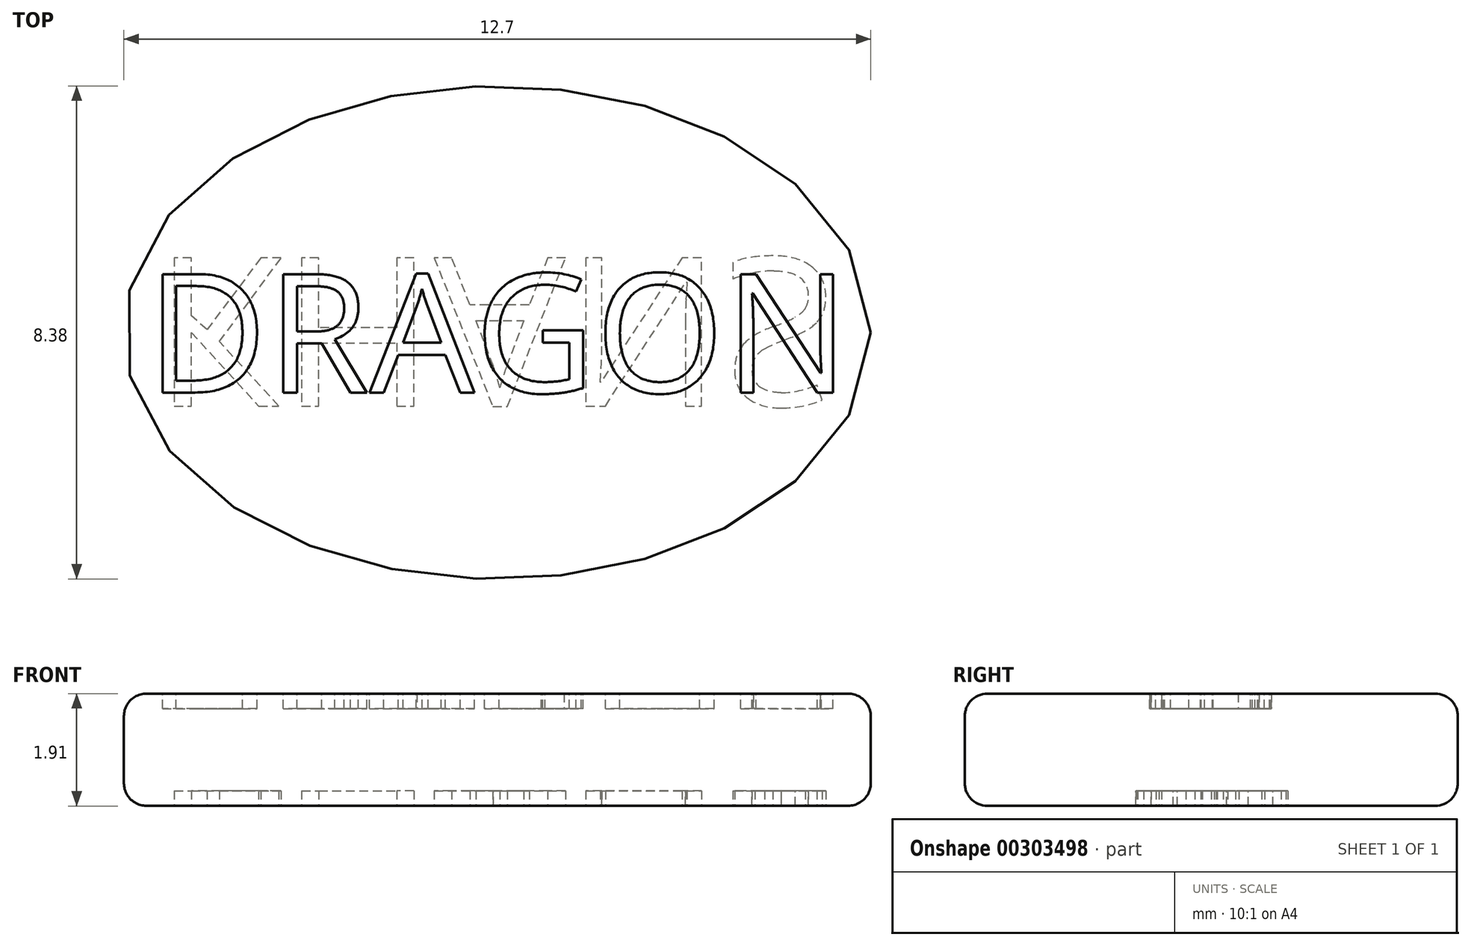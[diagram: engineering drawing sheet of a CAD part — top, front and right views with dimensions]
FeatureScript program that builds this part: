
annotation { "Feature Type Name" : "Feature", "Feature Type Description" : "" }
export const myFeature = defineFeature(function(context is Context, id is Id, definition is map)
    precondition{}
    {
        {
            var Q0;
            Q0=qCreatedBy(makeId("Top.planeOp"),FACE);
            var sketch = newSketch(context, id + "F0", { "sketchPlane" : qUnion([Q0])});
            skEllipse(sketch, "E0", {"center": v(0, 0) * mm, "majorRadius": 6.35 * mm, "minorRadius": 4.2 * mm, "majorAxis": v(1, 0)});
            skSolve(sketch);
        }
        {
            var Q0;
            Q0 = qSketchRegion(id + "F0", true);
            extrude(context, id + "F1", {"entities" : qUnion([Q0]), "oppositeDirection" : true, "depth" : 1.9 * mm});
        }
        {
            var Q0;
            Q0=makeQuery(id+"F1.opExtrude","CAP_FACE",FACE,{"disambiguationData":[OSD([sQuery(id+"F0.wireOp",EDGE,"E0")])],"isStart":true});
            var sketch = newSketch(context, id + "F2", { "sketchPlane" : qUnion([Q0])});
            skEllipse(sketch, "E1.0", {"center": v(0, 0) * mm, "majorRadius": 6.35 * mm, "minorRadius": 4.2 * mm, "majorAxis": v(1, 0)});
            skLineSegment(sketch, "E2", {"start": v(0, 0) * mm, "end": v(5.9, 0) * mm, "construction": true});
            skLineSegment(sketch, "E3", {"start": v(5.9, 0) * mm, "end": v(5.9, -1.02) * mm, "construction": true});
            skLineSegment(sketch, "E4", {"start": v(5.9, 0) * mm, "end": v(5.9, 1.02) * mm, "construction": true});
            skText(sketch, "E5", { "text": "DRAGON", "fontName": "OpenSans-Regular.ttf"});
            const initialGuessF2  = {"E5": [-0.00597, -0.00102, 1, 0, 0.00203]};
            skSetInitialGuess(sketch, initialGuessF2);
            skSolve(sketch);
        }
        {
            var Q0;
            Q0=makeQuery(id+"F1.opExtrude","CAP_FACE",FACE,{"disambiguationData":[OSD([sQuery(id+"F0.wireOp",EDGE,"E0")])],"isStart":false});
            var sketch = newSketch(context, id + "F3", { "sketchPlane" : qUnion([Q0])});
            skEllipse(sketch, "E6.0", {"center": v(0, 0) * mm, "majorRadius": 6.35 * mm, "minorRadius": 4.2 * mm, "majorAxis": v(1, 0)});
            skLineSegment(sketch, "E7", {"start": v(0, 0) * mm, "end": v(-5.84, 0) * mm, "construction": true});
            skLineSegment(sketch, "E8", {"start": v(-5.84, 0) * mm, "end": v(-5.84, 1.27) * mm, "construction": true});
            skLineSegment(sketch, "E9", {"start": v(-5.84, 0) * mm, "end": v(-5.84, -1.27) * mm});
            skText(sketch, "E10", { "text": "KHANS", "fontName": "OpenSans-Regular.ttf"});
            const initialGuessF3  = {"E10": [-0.00584, -0.00127, 1, 0, 0.00254]};
            skSetInitialGuess(sketch, initialGuessF3);
            skSolve(sketch);
        }
        {
            var Q0;
            Q0=makeQuery(id+"F2.imprint","IMPRINT",FACE,{"disambiguationData":[TD([[makeQuery(id+"F2.imprint","IMPRINT",EDGE,{"derivedFrom":sQuery(id+"F2.wireOp",EDGE,"E5.sketch_text.stroke-0")}),-1.0]])]});
            var Q1;
            Q1=makeQuery(id+"F2.imprint","IMPRINT",FACE,{"disambiguationData":[TD([[makeQuery(id+"F2.imprint","IMPRINT",EDGE,{"derivedFrom":sQuery(id+"F2.wireOp",EDGE,"E5.sketch_text.stroke-14")}),-1.0]])]});
            var Q2;
            Q2=makeQuery(id+"F2.imprint","IMPRINT",FACE,{"disambiguationData":[TD([[makeQuery(id+"F2.imprint","IMPRINT",EDGE,{"derivedFrom":sQuery(id+"F2.wireOp",EDGE,"E5.sketch_text.stroke-32")}),-1.0]])]});
            var Q3;
            Q3=makeQuery(id+"F2.imprint","IMPRINT",FACE,{"disambiguationData":[TD([[makeQuery(id+"F2.imprint","IMPRINT",EDGE,{"derivedFrom":sQuery(id+"F2.wireOp",EDGE,"E5.sketch_text.stroke-45")}),-1.0]])]});
            var Q4;
            Q4=makeQuery(id+"F2.imprint","IMPRINT",FACE,{"disambiguationData":[TD([[makeQuery(id+"F2.imprint","IMPRINT",EDGE,{"derivedFrom":sQuery(id+"F2.wireOp",EDGE,"E5.sketch_text.stroke-65")}),-1.0]])]});
            var Q5;
            Q5=makeQuery(id+"F2.imprint","IMPRINT",FACE,{"disambiguationData":[TD([[makeQuery(id+"F2.imprint","IMPRINT",EDGE,{"derivedFrom":sQuery(id+"F2.wireOp",EDGE,"E5.sketch_text.stroke-81")}),-1.0]])]});
            extrude(context, id + "F4", {"entities" : qUnion([Q0, Q1, Q2, Q3, Q4, Q5]), "operationType" : NewBodyOperationType.REMOVE, "oppositeDirection" : true, "depth" : 0.25 * mm});
        }
        {
            var Q0;
            Q0=makeQuery(id+"F3.imprint","IMPRINT",FACE,{"disambiguationData":[TD([[makeQuery(id+"F3.imprint","IMPRINT",EDGE,{"derivedFrom":sQuery(id+"F3.wireOp",EDGE,"E10.sketch_text.stroke-0")}),-1.0]])]});
            var Q1;
            Q1=makeQuery(id+"F3.imprint","IMPRINT",FACE,{"disambiguationData":[TD([[makeQuery(id+"F3.imprint","IMPRINT",EDGE,{"derivedFrom":sQuery(id+"F3.wireOp",EDGE,"E10.sketch_text.stroke-12")}),-1.0]])]});
            var Q2;
            Q2=makeQuery(id+"F3.imprint","IMPRINT",FACE,{"disambiguationData":[TD([[makeQuery(id+"F3.imprint","IMPRINT",EDGE,{"derivedFrom":sQuery(id+"F3.wireOp",EDGE,"E10.sketch_text.stroke-24")}),-1.0]])]});
            var Q3;
            Q3=makeQuery(id+"F3.imprint","IMPRINT",FACE,{"disambiguationData":[TD([[makeQuery(id+"F3.imprint","IMPRINT",EDGE,{"derivedFrom":sQuery(id+"F3.wireOp",EDGE,"E10.sketch_text.stroke-37")}),-1.0]])]});
            var Q4;
            Q4=makeQuery(id+"F3.imprint","IMPRINT",FACE,{"disambiguationData":[TD([[makeQuery(id+"F3.imprint","IMPRINT",EDGE,{"derivedFrom":sQuery(id+"F3.wireOp",EDGE,"E10.sketch_text.stroke-52")}),-1.0]])]});
            extrude(context, id + "F5", {"entities" : qUnion([Q0, Q1, Q2, Q3, Q4]), "operationType" : NewBodyOperationType.REMOVE, "oppositeDirection" : true, "depth" : 0.25 * mm});
        }
        {
            var Q0;
            Q0=makeQuery(id+"F1.opExtrude","CAP_EDGE",EDGE,{"disambiguationData":[OSD([sQuery(id+"F0.wireOp",EDGE,"E0")])],"isStart":false});
            var Q1;
            Q1=makeQuery(id+"F1.opExtrude","CAP_EDGE",EDGE,{"disambiguationData":[OSD([sQuery(id+"F0.wireOp",EDGE,"E0")])],"isStart":true});
            fillet(context, id + "F6", {"entities" : qUnion([Q0, Q1]), "radius" : 0.38 * mm, "tangentPropagation" : true, "allowEdgeOverflow" : false});
        }
    });
